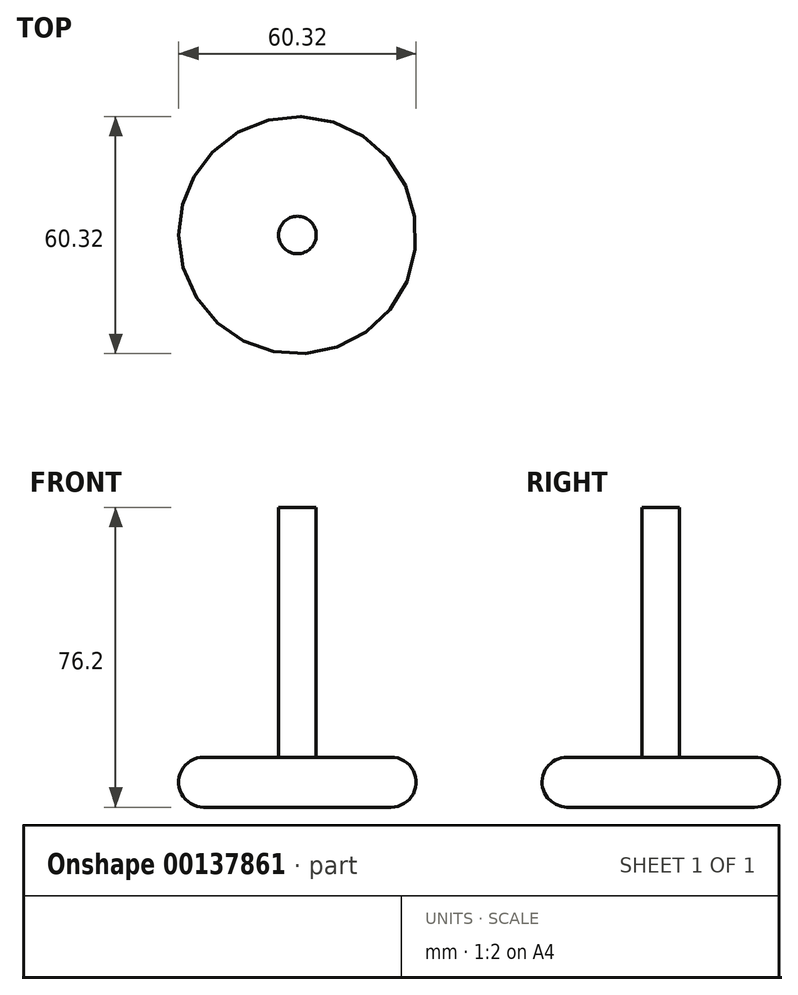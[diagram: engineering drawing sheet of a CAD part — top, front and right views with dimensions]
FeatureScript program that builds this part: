
annotation { "Feature Type Name" : "Feature", "Feature Type Description" : "" }
export const myFeature = defineFeature(function(context is Context, id is Id, definition is map)
    precondition{}
    {
        {
            var Q0;
            Q0=qCreatedBy(makeId("Front.planeOp"),FACE);
            var sketch = newSketch(context, id + "F0", { "sketchPlane" : qUnion([Q0])});
            skLineSegment(sketch, "E0", {"start": v(0, 0) * mm, "end": v(0, 76.2) * mm});
            skLineSegment(sketch, "E1", {"start": v(0, 76.2) * mm, "end": v(4.76, 76.2) * mm});
            skLineSegment(sketch, "E2", {"start": v(4.76, 76.2) * mm, "end": v(4.76, 12.7) * mm});
            skLineSegment(sketch, "E3", {"start": v(4.76, 12.7) * mm, "end": v(23.81, 12.7) * mm});
            skLineSegment(sketch, "E4", {"start": v(30.16, 6.35) * mm, "end": v(30.16, 6.35) * mm});
            skLineSegment(sketch, "E5", {"start": v(23.81, 0) * mm, "end": v(0, 0) * mm});
            skPoint(sketch, "E6.visualSharp", {"position": v(30.16, 12.7) * mm});
            skArc(sketch, "E6.filletArc", {"start": v(30.16, 6.35) * mm, "mid": v(28.3, 10.84) * mm, "end": v(23.81, 12.7) * mm});
            skPoint(sketch, "E7.visualSharp", {"position": v(30.16, 0) * mm});
            skArc(sketch, "E7.filletArc", {"start": v(23.81, 0) * mm, "mid": v(28.3, 1.86) * mm, "end": v(30.16, 6.35) * mm});
            skSolve(sketch);
        }
        {
            var Q0;
            Q0=qSketchRegion(id+"F0",true);
            var Q1;
            Q1=sQuery(id+"F0.wireOp",EDGE,"E0");
            revolve(context, id + "F1", {"entities" : qUnion([Q0]), "axis" : qUnion([Q1]), "revolveType" : RevolveType.FULL});
        }
    });
